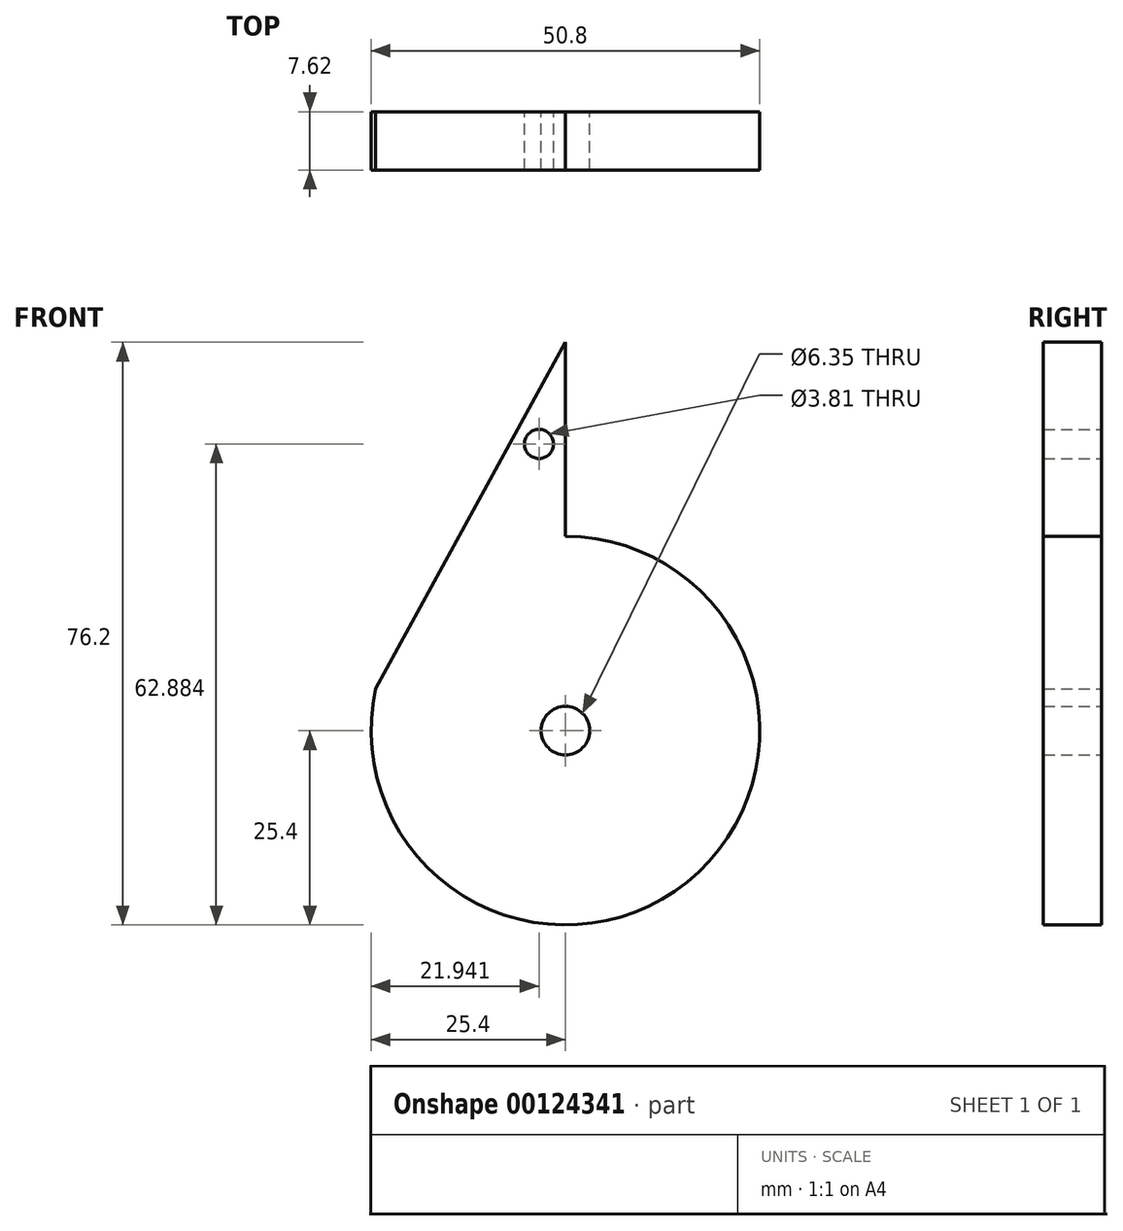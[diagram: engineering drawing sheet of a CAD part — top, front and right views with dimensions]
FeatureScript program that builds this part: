
annotation { "Feature Type Name" : "Feature", "Feature Type Description" : "" }
export const myFeature = defineFeature(function(context is Context, id is Id, definition is map)
    precondition{}
    {
        {
            var Q0;
            Q0=qCreatedBy(makeId("Front.planeOp"),FACE);
            var sketch = newSketch(context, id + "F0", { "sketchPlane" : qUnion([Q0])});
            skArc(sketch, "E0", {"start": v(-24.8, 5.45) * mm, "mid": v(15.92, -19.8) * mm, "end": v(0, 25.4) * mm});
            skLineSegment(sketch, "E1", {"start": v(0, 50.8) * mm, "end": v(-24.8, 5.45) * mm});
            skLineSegment(sketch, "E2", {"start": v(0, 50.8) * mm, "end": v(0, 25.4) * mm});
            skCircle(sketch, "E3", {"center": v(0, 0) * mm, "radius": 3.18 * mm});
            skCircle(sketch, "E4", {"center": v(-3.46, 37.48) * mm, "radius": 1.9 * mm});
            skSolve(sketch);
        }
        {
            var Q0;
            Q0 = qSketchRegion(id + "F0", true);
            extrude(context, id + "F1", {"entities" : qUnion([Q0]), "depth" : 7.62 * mm});
        }
    });
